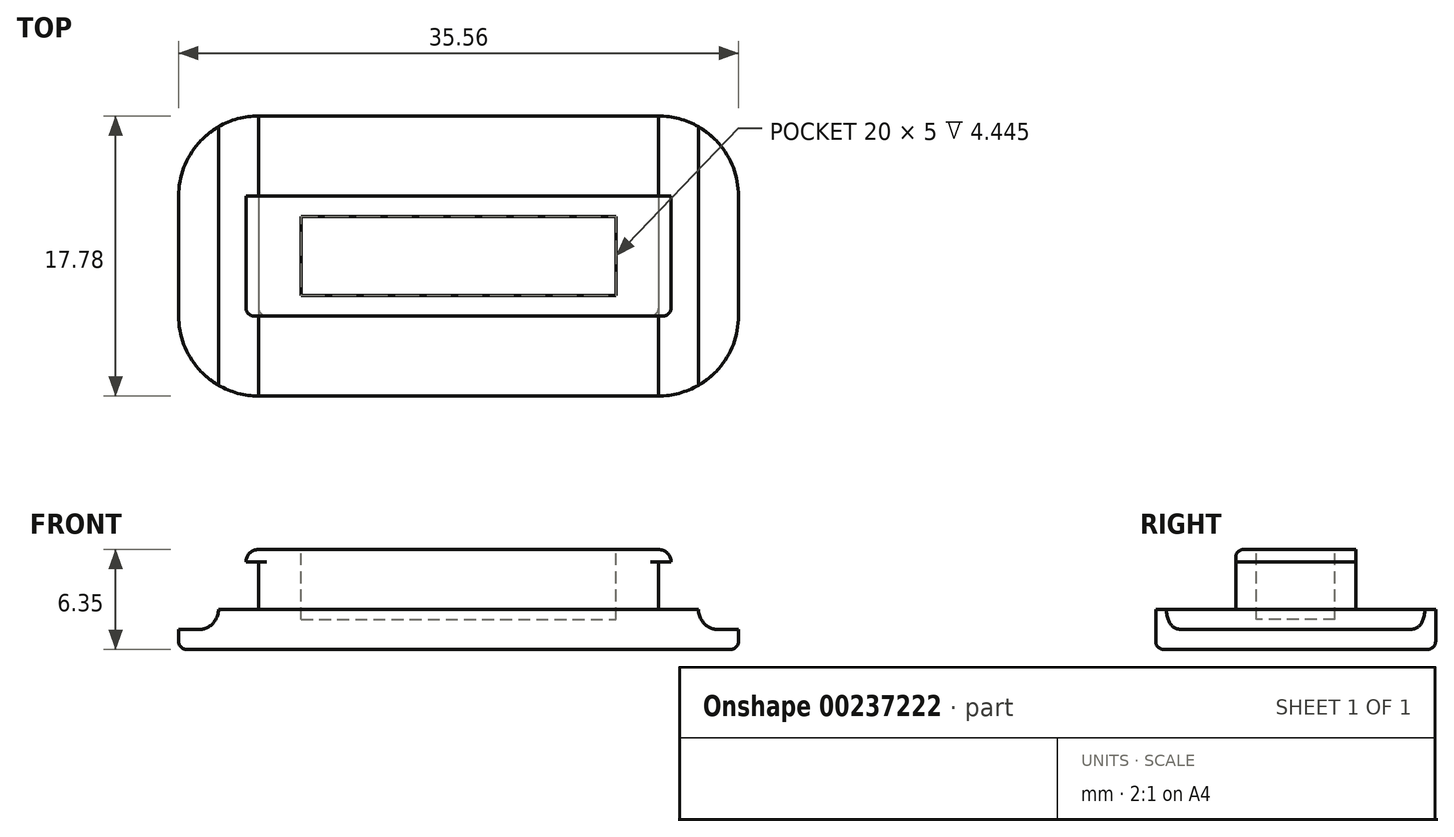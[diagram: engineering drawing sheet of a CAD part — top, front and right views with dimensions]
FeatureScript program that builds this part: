
annotation { "Feature Type Name" : "Feature", "Feature Type Description" : "" }
export const myFeature = defineFeature(function(context is Context, id is Id, definition is map)
    precondition{}
    {
        {
            var Q0;
            Q0=qCreatedBy(makeId("Top.planeOp"),FACE);
            var sketch = newSketch(context, id + "F0", { "sketchPlane" : qUnion([Q0])});
            skLineSegment(sketch, "E0.bottom", {"start": v(0, 0) * mm, "end": v(35.56, 0) * mm});
            skLineSegment(sketch, "E0.top", {"start": v(0, 17.78) * mm, "end": v(35.56, 17.78) * mm});
            skLineSegment(sketch, "E0.left", {"start": v(0, 0) * mm, "end": v(0, 17.78) * mm});
            skLineSegment(sketch, "E0.right", {"start": v(35.56, 0) * mm, "end": v(35.56, 17.78) * mm});
            skSolve(sketch);
        }
        {
            var Q0;
            Q0 = qSketchRegion(id + "F0", true);
            extrude(context, id + "F1", {"entities" : qUnion([Q0]), "depth" : 6.35 * mm});
        }
        {
            var Q0;
            Q0=makeQuery(id+"F1.opExtrude","SWEPT_FACE",FACE,{"disambiguationData":[OSD([sQuery(id+"F0.wireOp",EDGE,"E0.bottom")])]});
            var sketch = newSketch(context, id + "F2", { "sketchPlane" : qUnion([Q0])});
            skLineSegment(sketch, "E1", {"start": v(31.28, 5.55) * mm, "end": v(30.48, 5.55) * mm});
            skLineSegment(sketch, "E2", {"start": v(30.48, 5.55) * mm, "end": v(30.48, 2.54) * mm});
            skLineSegment(sketch, "E3", {"start": v(30.48, 2.54) * mm, "end": v(33.02, 2.54) * mm});
            skLineSegment(sketch, "E4", {"start": v(31.28, 5.55) * mm, "end": v(31.28, 5.55) * mm});
            skLineSegment(sketch, "E5", {"start": v(31.28, 6.35) * mm, "end": v(35.56, 6.35) * mm});
            skLineSegment(sketch, "E6", {"start": v(35.56, 6.35) * mm, "end": v(35.56, 2.54) * mm});
            skLineSegment(sketch, "E7", {"start": v(17.78, 6.35) * mm, "end": v(17.78, 0) * mm, "construction": true});
            skLineSegment(sketch, "E8.MirrorCS", {"start": v(4.28, 5.55) * mm, "end": v(4.28, 5.55) * mm});
            skLineSegment(sketch, "E9.MirrorCS", {"start": v(4.28, 5.55) * mm, "end": v(5.08, 5.55) * mm});
            skLineSegment(sketch, "E10.MirrorCS", {"start": v(5.08, 5.55) * mm, "end": v(5.08, 2.54) * mm});
            skLineSegment(sketch, "E11.MirrorCS", {"start": v(5.08, 2.54) * mm, "end": v(2.54, 2.54) * mm});
            skLineSegment(sketch, "E12.MirrorCS", {"start": v(0, 6.35) * mm, "end": v(0, 2.54) * mm});
            skLineSegment(sketch, "E13.MirrorCS", {"start": v(4.28, 6.35) * mm, "end": v(0, 6.35) * mm});
            skLineSegment(sketch, "E14.top", {"start": v(30.48, 6.35) * mm, "end": v(30.48, 6.35) * mm});
            skPoint(sketch, "E15.visualSharp", {"position": v(31.28, 6.35) * mm});
            skArc(sketch, "E15.filletArc", {"start": v(31.28, 5.55) * mm, "mid": v(31.05, 6.12) * mm, "end": v(30.48, 6.35) * mm});
            skLineSegment(sketch, "E16", {"start": v(30.48, 6.35) * mm, "end": v(31.28, 6.35) * mm});
            skArc(sketch, "E17.MirrorCS", {"start": v(4.28, 5.55) * mm, "mid": v(4.51, 6.12) * mm, "end": v(5.08, 6.35) * mm});
            skLineSegment(sketch, "E18", {"start": v(4.28, 6.35) * mm, "end": v(5.08, 6.35) * mm});
            skLineSegment(sketch, "E19.top", {"start": v(35.56, 1.27) * mm, "end": v(34.3, 1.27) * mm});
            skLineSegment(sketch, "E19.left", {"start": v(35.56, 2.54) * mm, "end": v(35.56, 1.27) * mm});
            skLineSegment(sketch, "E19.right", {"start": v(33.02, 2.54) * mm, "end": v(33.02, 2.54) * mm});
            skPoint(sketch, "E20.visualSharp", {"position": v(33.02, 1.27) * mm});
            skArc(sketch, "E20.filletArc", {"start": v(33.02, 2.54) * mm, "mid": v(33.4, 1.64) * mm, "end": v(34.3, 1.27) * mm});
            skArc(sketch, "E21.MirrorCS", {"start": v(2.54, 2.54) * mm, "mid": v(2.17, 1.64) * mm, "end": v(1.27, 1.27) * mm});
            skLineSegment(sketch, "E22.MirrorCS", {"start": v(0, 2.54) * mm, "end": v(0, 1.27) * mm});
            skLineSegment(sketch, "E23.MirrorCS", {"start": v(0, 1.27) * mm, "end": v(1.27, 1.27) * mm});
            skSolve(sketch);
        }
        {
            var Q0;
            Q0 = qSketchRegion(id + "F2", true);
            extrude(context, id + "F3", {"entities" : qUnion([Q0]), "operationType" : NewBodyOperationType.REMOVE, "oppositeDirection" : true, "depth" : 25.4 * mm});
        }
        {
            var Q0;
            Q0=makeQuery(id+"F1.opExtrude","SWEPT_FACE",FACE,{"disambiguationData":[OSD([sQuery(id+"F0.wireOp",EDGE,"E0.right")])]});
            var sketch = newSketch(context, id + "F4", { "sketchPlane" : qUnion([Q0])});
            skLineSegment(sketch, "E24.bottom", {"start": v(0, 2.56) * mm, "end": v(5.08, 2.56) * mm});
            skLineSegment(sketch, "E24.top", {"start": v(0, 6.57) * mm, "end": v(5.08, 6.57) * mm});
            skLineSegment(sketch, "E24.left", {"start": v(0, 2.56) * mm, "end": v(0, 6.57) * mm});
            skLineSegment(sketch, "E24.right", {"start": v(5.08, 2.56) * mm, "end": v(5.08, 6.57) * mm});
            skLineSegment(sketch, "E25", {"start": v(8.89, 7.23) * mm, "end": v(8.89, 0) * mm, "construction": true});
            skLineSegment(sketch, "E26.MirrorCS", {"start": v(12.7, 2.56) * mm, "end": v(12.7, 6.57) * mm});
            skLineSegment(sketch, "E27.MirrorCS", {"start": v(17.78, 6.57) * mm, "end": v(12.7, 6.57) * mm});
            skLineSegment(sketch, "E28.MirrorCS", {"start": v(17.78, 2.56) * mm, "end": v(17.78, 6.57) * mm});
            skLineSegment(sketch, "E29.MirrorCS", {"start": v(17.78, 2.56) * mm, "end": v(12.7, 2.56) * mm});
            skSolve(sketch);
        }
        {
            var Q0;
            Q0 = qSketchRegion(id + "F4", true);
            extrude(context, id + "F5", {"entities" : qUnion([Q0]), "operationType" : NewBodyOperationType.REMOVE, "oppositeDirection" : true, "depth" : 50.8 * mm});
        }
        {
            var Q0;
            Q0=makeQuery(id+"F1.opExtrude","CAP_FACE",FACE,{"disambiguationData":[OSD([sQuery(id+"F0.wireOp",EDGE,"E0.bottom"),sQuery(id+"F0.wireOp",EDGE,"E0.top"),sQuery(id+"F0.wireOp",EDGE,"E0.left"),sQuery(id+"F0.wireOp",EDGE,"E0.right")])],"isStart":false});
            var sketch = newSketch(context, id + "F6", { "sketchPlane" : qUnion([Q0])});
            skLineSegment(sketch, "E30.bottom", {"start": v(7.78, 11.4) * mm, "end": v(27.78, 11.4) * mm});
            skLineSegment(sketch, "E30.top", {"start": v(7.78, 6.4) * mm, "end": v(27.78, 6.4) * mm});
            skLineSegment(sketch, "E30.left", {"start": v(7.78, 11.4) * mm, "end": v(7.78, 6.4) * mm});
            skLineSegment(sketch, "E30.right", {"start": v(27.78, 11.4) * mm, "end": v(27.78, 6.4) * mm});
            skLineSegment(sketch, "E31", {"start": v(17.78, 5.08) * mm, "end": v(17.78, 5.08) * mm});
            skPoint(sketch, "E32", {"position": v(17.78, 11.4) * mm});
            skLineSegment(sketch, "E33", {"start": v(5.08, 8.9) * mm, "end": v(30.48, 8.9) * mm, "construction": true});
            skPoint(sketch, "E34", {"position": v(27.78, 8.9) * mm});
            skSolve(sketch);
        }
        {
            var Q0;
            Q0 = qSketchRegion(id + "F6", true);
            var Q1;
            Q1=makeQuery(id+"F5.boolean.opBoolean","MERGE",FACE,{"derivedFrom":[makeQuery(id+"F3.boolean.opBoolean","COPY",FACE,{"derivedFrom":makeQuery(id+"F3.opExtrude","SWEPT_FACE",FACE,{"disambiguationData":[OSD([sQuery(id+"F2.wireOp",EDGE,"E3")])]})}),makeQuery(id+"F3.boolean.opBoolean","COPY",FACE,{"derivedFrom":makeQuery(id+"F3.opExtrude","SWEPT_FACE",FACE,{"disambiguationData":[OSD([sQuery(id+"F2.wireOp",EDGE,"E11.MirrorCS")])]})}),makeQuery(id+"F5.opExtrude","SWEPT_FACE",FACE,{"disambiguationData":[OSD([sQuery(id+"F4.wireOp",EDGE,"E24.bottom")])]}),makeQuery(id+"F5.opExtrude","SWEPT_FACE",FACE,{"disambiguationData":[OSD([sQuery(id+"F4.wireOp",EDGE,"A8vW1MZ6-efqk-OqLK-yjxq-DQb5dltrwmxJ.bottom")])]})]});
            extrude(context, id + "F7", {"entities" : qUnion([Q0]), "operationType" : NewBodyOperationType.REMOVE, "endBound" : BoundingType.UP_TO_SURFACE, "oppositeDirection" : true, "endBoundEntityFace" : qUnion([Q1]), "depth" : 25.4 * mm});
        }
        {
            var Q0;
            Q0=makeQuery(id+"F7.boolean.opBoolean","COPY",FACE,{"derivedFrom":makeQuery(id+"F7.opExtrude","CAP_FACE",FACE,{"disambiguationData":[OSD([sQuery(id+"F6.wireOp",EDGE,"E30.bottom"),sQuery(id+"F6.wireOp",EDGE,"E30.top"),sQuery(id+"F6.wireOp",EDGE,"E30.left"),sQuery(id+"F6.wireOp",EDGE,"E30.right")])],"isStart":false})});
            var sketch = newSketch(context, id + "F8", { "sketchPlane" : qUnion([Q0])});
            skLineSegment(sketch, "E35.bottom", {"start": v(27.78, 6.4) * mm, "end": v(7.78, 6.4) * mm});
            skLineSegment(sketch, "E35.top", {"start": v(27.78, 11.4) * mm, "end": v(7.78, 11.4) * mm});
            skLineSegment(sketch, "E35.left", {"start": v(27.78, 6.4) * mm, "end": v(27.78, 11.4) * mm});
            skLineSegment(sketch, "E35.right", {"start": v(7.78, 6.4) * mm, "end": v(7.78, 11.4) * mm});
            skSolve(sketch);
        }
        {
            var Q0;
            Q0 = qSketchRegion(id + "F8", true);
            extrude(context, id + "F9", {"entities" : qUnion([Q0]), "operationType" : NewBodyOperationType.REMOVE, "oppositeDirection" : true, "depth" : 0.64 * mm});
        }
        {
            var Q0;
            Q0=makeQuery(id+"F1.opExtrude","SWEPT_EDGE",EDGE,{"disambiguationData":[OSD([sQuery(id+"F0.wireOp",EDGE,"E0.bottom"),sQuery(id+"F0.wireOp",EDGE,"E0.left")])]});
            var Q1;
            Q1=makeQuery(id+"F1.opExtrude","SWEPT_EDGE",EDGE,{"disambiguationData":[OSD([sQuery(id+"F0.wireOp",EDGE,"E0.bottom"),sQuery(id+"F0.wireOp",EDGE,"E0.right")])]});
            var Q2;
            Q2=makeQuery(id+"F1.opExtrude","SWEPT_EDGE",EDGE,{"disambiguationData":[OSD([sQuery(id+"F0.wireOp",EDGE,"E0.top"),sQuery(id+"F0.wireOp",EDGE,"E0.right")])]});
            var Q3;
            Q3=makeQuery(id+"F1.opExtrude","SWEPT_EDGE",EDGE,{"disambiguationData":[OSD([sQuery(id+"F0.wireOp",EDGE,"E0.top"),sQuery(id+"F0.wireOp",EDGE,"E0.left")])]});
            fillet(context, id + "F10", {"entities" : qUnion([Q0, Q1, Q2, Q3]), "radius" : 5.08 * mm, "tangentPropagation" : true, "allowEdgeOverflow" : false});
        }
        {
            var Q0;
            Q0=makeQuery(id+"F5.boolean.opBoolean","MERGE",EDGE,{"derivedFrom":[makeQuery(id+"F3.boolean.opBoolean","COPY",EDGE,{"derivedFrom":makeQuery(id+"F3.opExtrude","CAP_EDGE",EDGE,{"disambiguationData":[OSD([sQuery(id+"F2.wireOp",EDGE,"E3")])],"isStart":true})}),makeQuery(id+"F3.boolean.opBoolean","COPY",EDGE,{"derivedFrom":makeQuery(id+"F3.opExtrude","CAP_EDGE",EDGE,{"disambiguationData":[OSD([sQuery(id+"F2.wireOp",EDGE,"E11.MirrorCS")])],"isStart":true})}),makeQuery(id+"F5.opExtrude","SWEPT_EDGE",EDGE,{"disambiguationData":[OSD([sQuery(id+"F0.wireOp",EDGE,"E0.bottom"),sQuery(id+"F0.wireOp",EDGE,"E0.right"),sQuery(id+"F4.wireOp",EDGE,"E24.bottom"),sQuery(id+"F4.wireOp",EDGE,"E24.left")])]})]});
            var Q1;
            Q1=makeQuery(id+"F1.opExtrude","CAP_EDGE",EDGE,{"disambiguationData":[OSD([sQuery(id+"F0.wireOp",EDGE,"E0.bottom")])],"isStart":true});
            var Q2;
            Q2=makeQuery(id+"F5.boolean.opBoolean","INTERSECT",EDGE,{"derivedFrom":[makeQuery(id+"F3.boolean.opBoolean","COPY",FACE,{"derivedFrom":makeQuery(id+"F3.opExtrude","SWEPT_FACE",FACE,{"disambiguationData":[OSD([sQuery(id+"F2.wireOp",EDGE,"E10.MirrorCS")])]})}),makeQuery(id+"F5.opExtrude","SWEPT_FACE",FACE,{"disambiguationData":[OSD([sQuery(id+"F4.wireOp",EDGE,"E24.right")])]})]});
            var Q3;
            Q3=makeQuery(id+"F5.boolean.opBoolean","INTERSECT",EDGE,{"derivedFrom":[makeQuery(id+"F1.opExtrude","CAP_FACE",FACE,{"disambiguationData":[OSD([sQuery(id+"F0.wireOp",EDGE,"E0.bottom"),sQuery(id+"F0.wireOp",EDGE,"E0.top"),sQuery(id+"F0.wireOp",EDGE,"E0.left"),sQuery(id+"F0.wireOp",EDGE,"E0.right")])],"isStart":false}),makeQuery(id+"F5.opExtrude","SWEPT_FACE",FACE,{"disambiguationData":[OSD([sQuery(id+"F4.wireOp",EDGE,"E24.right")])]})]});
            var Q4;
            Q4=makeQuery(id+"F5.boolean.opBoolean","INTERSECT",EDGE,{"derivedFrom":[makeQuery(id+"F1.opExtrude","CAP_FACE",FACE,{"disambiguationData":[OSD([sQuery(id+"F0.wireOp",EDGE,"E0.bottom"),sQuery(id+"F0.wireOp",EDGE,"E0.top"),sQuery(id+"F0.wireOp",EDGE,"E0.left"),sQuery(id+"F0.wireOp",EDGE,"E0.right")])],"isStart":false}),makeQuery(id+"F5.opExtrude","SWEPT_FACE",FACE,{"disambiguationData":[OSD([sQuery(id+"F4.wireOp",EDGE,"A8vW1MZ6-efqk-OqLK-yjxq-DQb5dltrwmxJ.right")])]})]});
            var Q5;
            Q5=makeQuery(id+"F5.boolean.opBoolean","INTERSECT",EDGE,{"derivedFrom":[makeQuery(id+"F3.boolean.opBoolean","COPY",FACE,{"derivedFrom":makeQuery(id+"F3.opExtrude","SWEPT_FACE",FACE,{"disambiguationData":[OSD([sQuery(id+"F2.wireOp",EDGE,"E2")])]})}),makeQuery(id+"F5.opExtrude","SWEPT_FACE",FACE,{"disambiguationData":[OSD([sQuery(id+"F4.wireOp",EDGE,"E24.right")])]})]});
            var Q6;
            Q6=makeQuery(id+"F5.boolean.opBoolean","INTERSECT",EDGE,{"derivedFrom":[makeQuery(id+"F3.boolean.opBoolean","COPY",FACE,{"derivedFrom":makeQuery(id+"F3.opExtrude","SWEPT_FACE",FACE,{"disambiguationData":[OSD([sQuery(id+"F2.wireOp",EDGE,"E10.MirrorCS")])]})}),makeQuery(id+"F5.opExtrude","SWEPT_FACE",FACE,{"disambiguationData":[OSD([sQuery(id+"F4.wireOp",EDGE,"A8vW1MZ6-efqk-OqLK-yjxq-DQb5dltrwmxJ.right")])]})]});
            var Q7;
            Q7=makeQuery(id+"F5.boolean.opBoolean","INTERSECT",EDGE,{"derivedFrom":[makeQuery(id+"F3.boolean.opBoolean","COPY",FACE,{"derivedFrom":makeQuery(id+"F3.opExtrude","SWEPT_FACE",FACE,{"disambiguationData":[OSD([sQuery(id+"F2.wireOp",EDGE,"E2")])]})}),makeQuery(id+"F5.opExtrude","SWEPT_FACE",FACE,{"disambiguationData":[OSD([sQuery(id+"F4.wireOp",EDGE,"A8vW1MZ6-efqk-OqLK-yjxq-DQb5dltrwmxJ.right")])]})]});
            fillet(context, id + "F11", {"entities" : qUnion([Q0, Q1, Q2, Q3, Q4, Q5, Q6, Q7]), "radius" : 0.5 * mm, "tangentPropagation" : true, "allowEdgeOverflow" : false});
        }
    });
